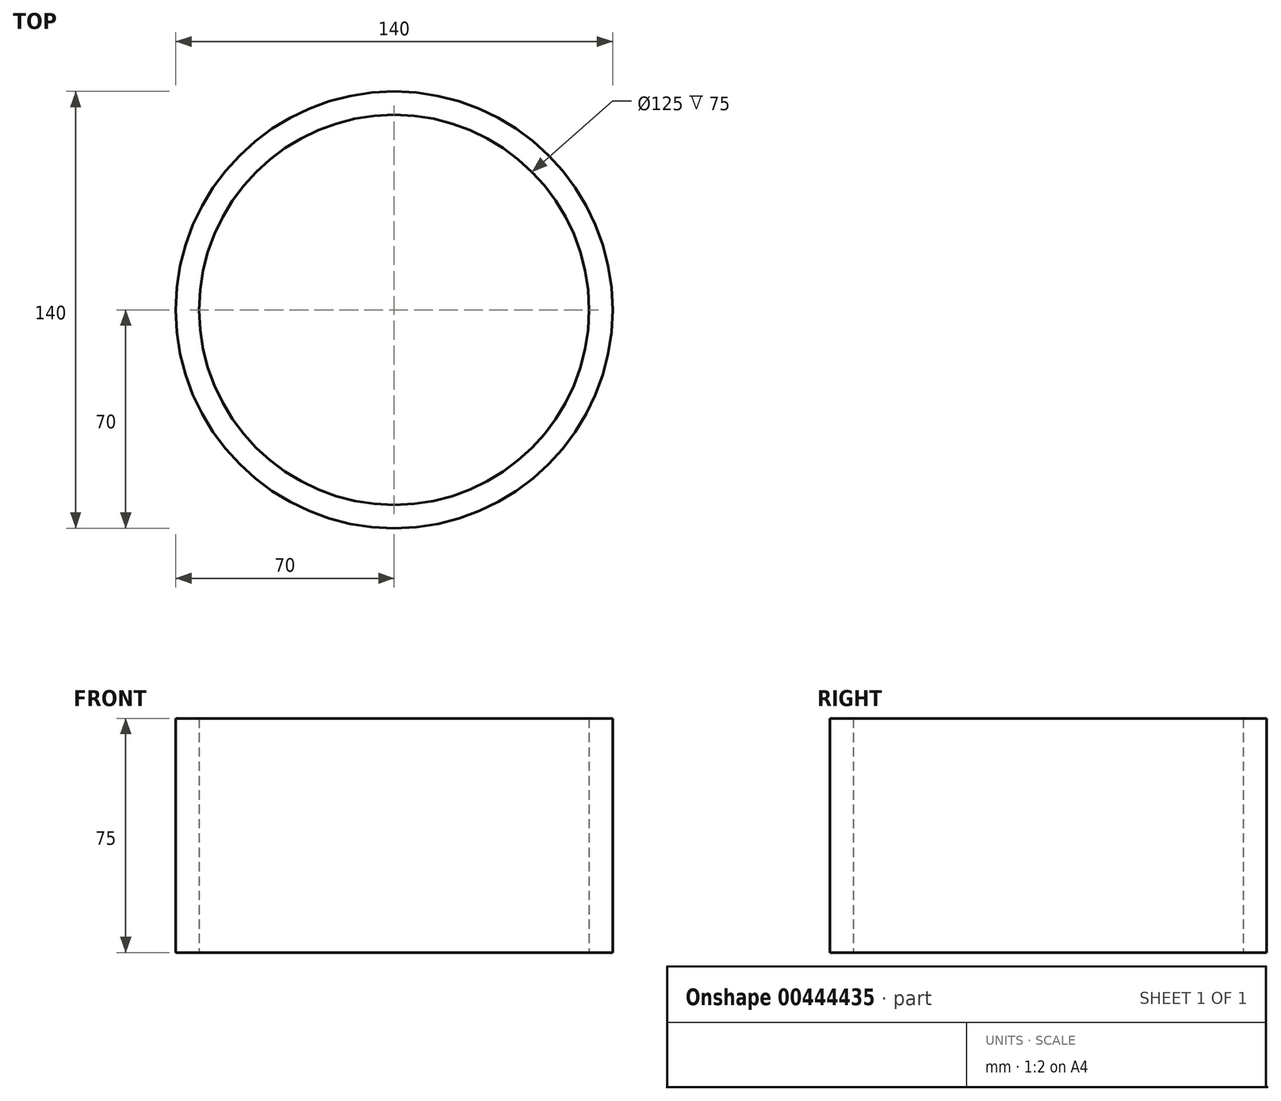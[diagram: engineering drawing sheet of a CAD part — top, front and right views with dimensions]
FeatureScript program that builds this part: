
annotation { "Feature Type Name" : "Feature", "Feature Type Description" : "" }
export const myFeature = defineFeature(function(context is Context, id is Id, definition is map)
    precondition{}
    {
        {
            var Q0;
            Q0=qCreatedBy(makeId("Top.planeOp"),FACE);
            var sketch = newSketch(context, id + "F0", { "sketchPlane" : qUnion([Q0])});
            skCircle(sketch, "E0", {"center": v(0, 0) * mm, "radius": 70 * mm});
            skCircle(sketch, "E1", {"center": v(0, 0) * mm, "radius": 62.5 * mm});
            skSolve(sketch);
        }
        {
            var Q0;
            Q0=makeQuery(id+"F0.imprint","IMPRINT",FACE,{"disambiguationData":[TD([[makeQuery(id+"F0.imprint","IMPRINT",EDGE,{"derivedFrom":sQuery(id+"F0.wireOp",EDGE,"E0")}),1.0]])]});
            extrude(context, id + "F1", {"entities" : qUnion([Q0]), "depth" : 75 * mm, "offsetDistance" : 25 * mm});
        }
    });
